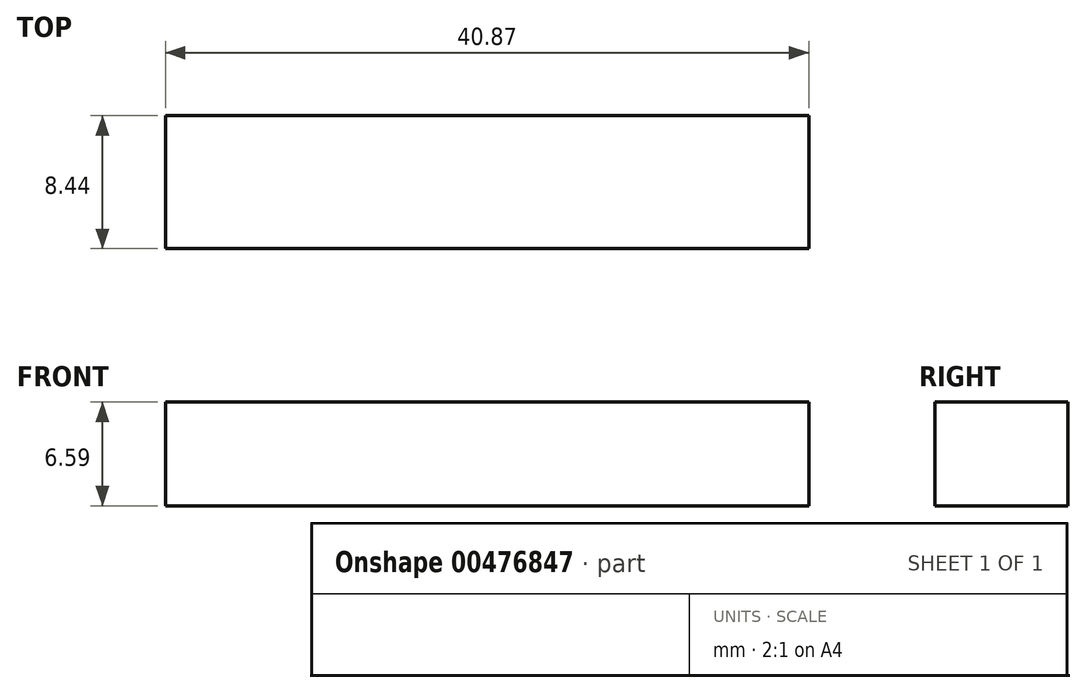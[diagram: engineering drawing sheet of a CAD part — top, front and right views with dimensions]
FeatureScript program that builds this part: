
annotation { "Feature Type Name" : "Feature", "Feature Type Description" : "" }
export const myFeature = defineFeature(function(context is Context, id is Id, definition is map)
    precondition{}
    {
        {
            var Q0;
            Q0=qCreatedBy(makeId("Right.planeOp"),FACE);
            var sketch = newSketch(context, id + "F0", { "sketchPlane" : qUnion([Q0])});
            skLineSegment(sketch, "E0.bottom", {"start": v(8.44, 0) * mm, "end": v(0, 0) * mm});
            skLineSegment(sketch, "E0.top", {"start": v(8.44, 6.59) * mm, "end": v(0, 6.59) * mm});
            skLineSegment(sketch, "E0.left", {"start": v(8.44, 0) * mm, "end": v(8.44, 6.59) * mm});
            skLineSegment(sketch, "E0.right", {"start": v(0, 0) * mm, "end": v(0, 6.59) * mm});
            skSolve(sketch);
        }
        {
            var Q0;
            Q0=makeQuery(id+"F0.imprint","IMPRINT",FACE,{"disambiguationData":[TD([[makeQuery(id+"F0.imprint","IMPRINT",EDGE,{"derivedFrom":sQuery(id+"F0.wireOp",EDGE,"E0.bottom")}),-1.0]])]});
            extrude(context, id + "F1", {"entities" : qUnion([Q0]), "depth" : 40.87 * mm});
        }
    });
